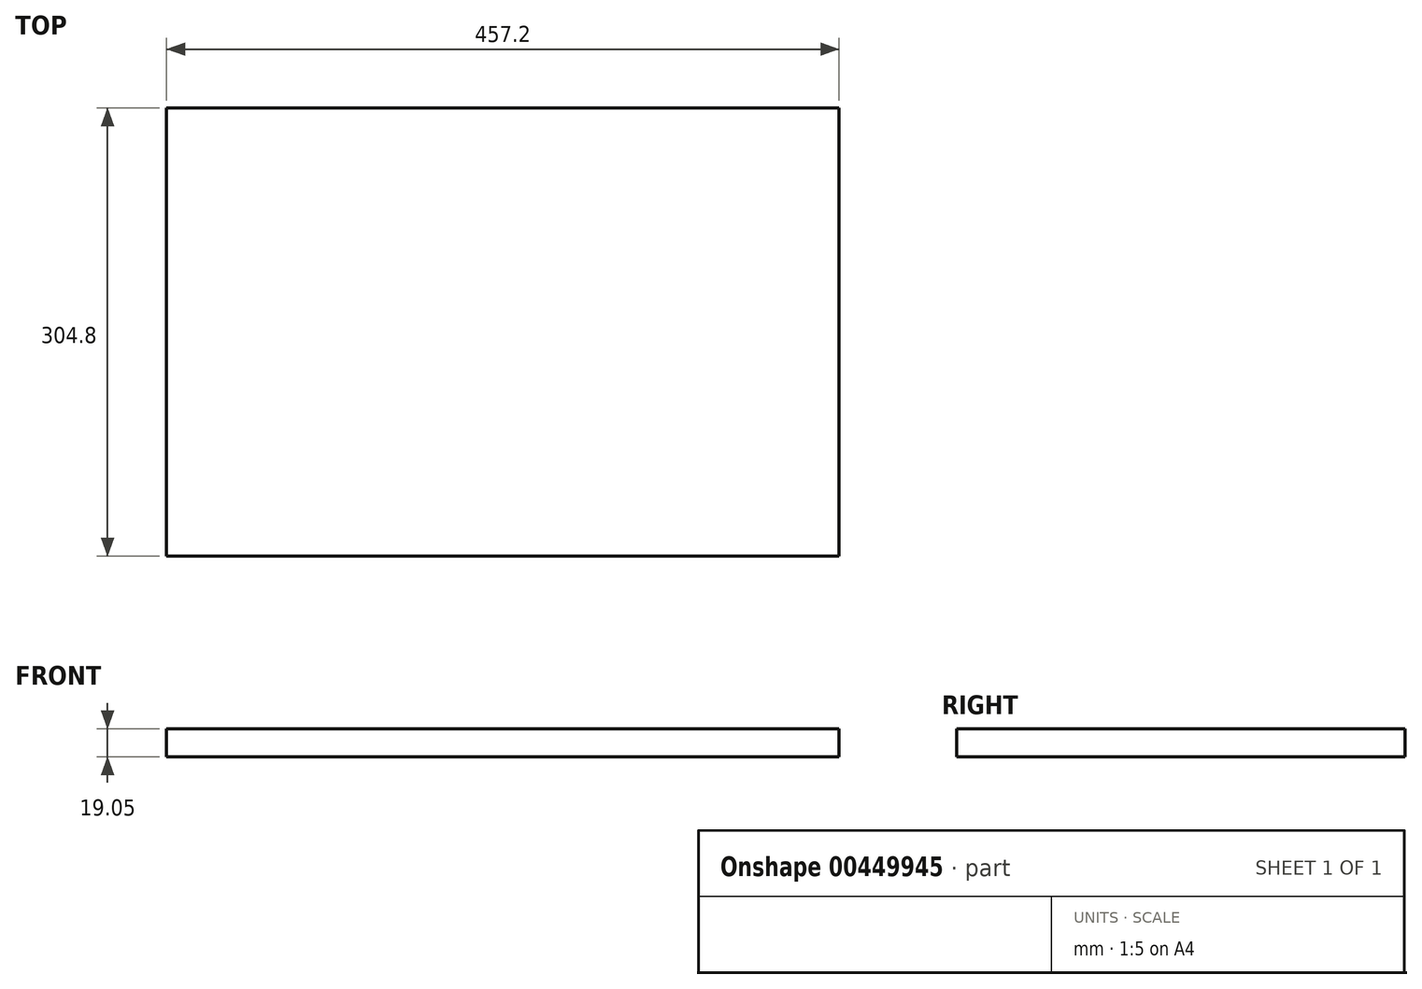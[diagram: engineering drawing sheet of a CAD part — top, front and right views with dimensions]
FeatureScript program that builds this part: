
annotation { "Feature Type Name" : "Feature", "Feature Type Description" : "" }
export const myFeature = defineFeature(function(context is Context, id is Id, definition is map)
    precondition{}
    {
        {
            var Q0;
            Q0=qCreatedBy(makeId("Top.planeOp"),FACE);
            var sketch = newSketch(context, id + "F0", { "sketchPlane" : qUnion([Q0])});
            skLineSegment(sketch, "E0.bottom", {"start": v(228.6, 152.4) * mm, "end": v(-228.6, 152.4) * mm});
            skLineSegment(sketch, "E0.top", {"start": v(228.6, -152.4) * mm, "end": v(-228.6, -152.4) * mm});
            skLineSegment(sketch, "E0.left", {"start": v(228.6, 152.4) * mm, "end": v(228.6, -152.4) * mm});
            skLineSegment(sketch, "E0.right", {"start": v(-228.6, 152.4) * mm, "end": v(-228.6, -152.4) * mm});
            skPoint(sketch, "E0.middle", {"position": v(0, 0) * mm});
            skSolve(sketch);
        }
        {
            var Q0;
            Q0=qSketchRegion(id+"F0",true);
            extrude(context, id + "F1", {"entities" : qUnion([Q0]), "depth" : 19.05 * mm});
        }
    });
